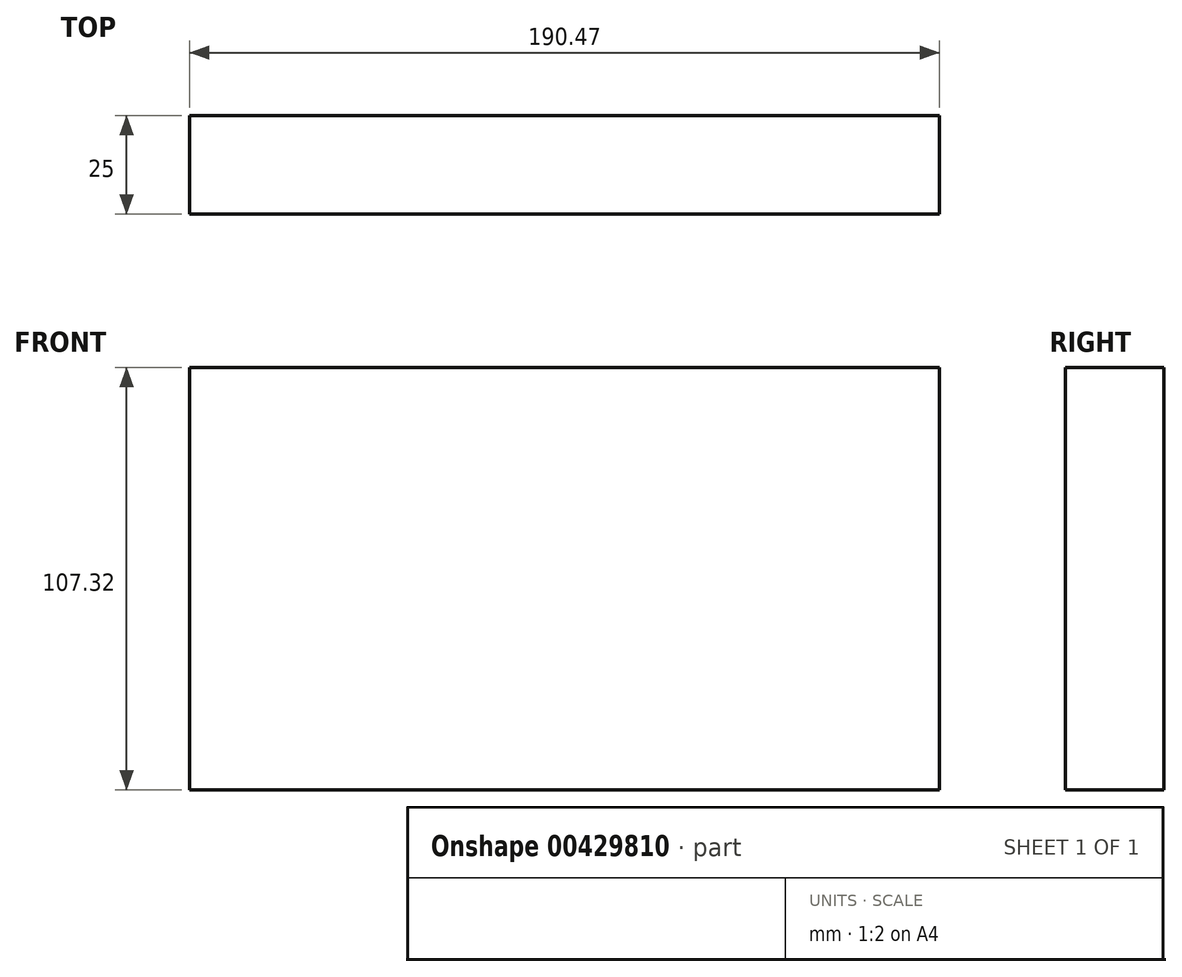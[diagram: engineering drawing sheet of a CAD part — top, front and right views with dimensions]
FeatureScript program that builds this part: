
annotation { "Feature Type Name" : "Feature", "Feature Type Description" : "" }
export const myFeature = defineFeature(function(context is Context, id is Id, definition is map)
    precondition{}
    {
        {
            var Q0;
            Q0=qCreatedBy(makeId("Front.planeOp"),FACE);
            var sketch = newSketch(context, id + "F0", { "sketchPlane" : qUnion([Q0])});
            skLineSegment(sketch, "E0.bottom", {"start": v(-90.82, 51.99) * mm, "end": v(99.65, 51.99) * mm});
            skLineSegment(sketch, "E0.top", {"start": v(-90.82, -55.33) * mm, "end": v(99.65, -55.33) * mm});
            skLineSegment(sketch, "E0.left", {"start": v(-90.82, 51.99) * mm, "end": v(-90.82, -55.33) * mm});
            skLineSegment(sketch, "E0.right", {"start": v(99.65, 51.99) * mm, "end": v(99.65, -55.33) * mm});
            skSolve(sketch);
        }
        {
            var Q0;
            Q0 = qSketchRegion(id + "F0", true);
            extrude(context, id + "F1", {"entities" : qUnion([Q0]), "depth" : 25 * mm});
        }
    });
